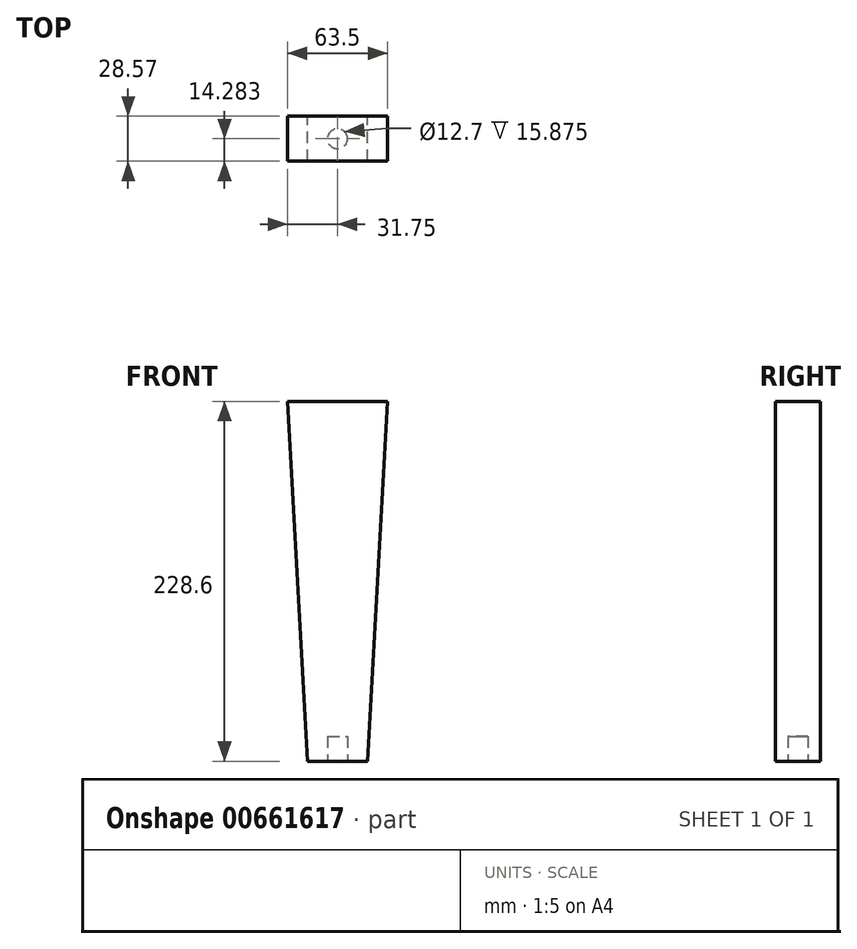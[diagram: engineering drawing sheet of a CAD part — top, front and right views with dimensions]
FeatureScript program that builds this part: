
annotation { "Feature Type Name" : "Feature", "Feature Type Description" : "" }
export const myFeature = defineFeature(function(context is Context, id is Id, definition is map)
    precondition{}
    {
        {
            var Q0;
            Q0=qCreatedBy(makeId("Front.planeOp"),FACE);
            var sketch = newSketch(context, id + "F0", { "sketchPlane" : qUnion([Q0])});
            skLineSegment(sketch, "E0.bottom", {"start": v(-31.75, 114.3) * mm, "end": v(31.75, 114.3) * mm});
            skLineSegment(sketch, "E0.top", {"start": v(-19.05, -114.3) * mm, "end": v(19.05, -114.3) * mm});
            skPoint(sketch, "E0.middle", {"position": v(0, 0) * mm});
            skLineSegment(sketch, "E1", {"start": v(-31.75, 114.3) * mm, "end": v(-19.05, -114.3) * mm});
            skLineSegment(sketch, "E2", {"start": v(31.75, 114.3) * mm, "end": v(19.05, -114.3) * mm});
            skSolve(sketch);
        }
        {
            var Q0;
            Q0=makeQuery(id+"F0.imprint","IMPRINT",FACE,{"disambiguationData":[TD([[makeQuery(id+"F0.imprint","IMPRINT",EDGE,{"derivedFrom":sQuery(id+"F0.wireOp",EDGE,"E0.bottom")}),-1.0]])]});
            extrude(context, id + "F1", {"entities" : qUnion([Q0]), "depth" : 28.57 * mm, "offsetDistance" : 25.4 * mm});
        }
        {
            var Q0;
            Q0=makeQuery(id+"F1.opExtrude","SWEPT_FACE",FACE,{"disambiguationData":[OSD([sQuery(id+"F0.wireOp",EDGE,"E0.top")])]});
            var sketch = newSketch(context, id + "F2", { "sketchPlane" : qUnion([Q0])});
            skCircle(sketch, "E3", {"center": v(0, 14.29) * mm, "radius": 6.35 * mm});
            skSolve(sketch);
        }
        {
            var Q0;
            Q0=makeQuery(id+"F2.imprint","IMPRINT",FACE,{"disambiguationData":[TD([[makeQuery(id+"F2.imprint","IMPRINT",EDGE,{"derivedFrom":sQuery(id+"F2.wireOp",EDGE,"E3")}),1.0]])]});
            extrude(context, id + "F3", {"entities" : qUnion([Q0]), "operationType" : NewBodyOperationType.REMOVE, "oppositeDirection" : true, "depth" : 15.88 * mm, "offsetDistance" : 25.4 * mm});
        }
    });
